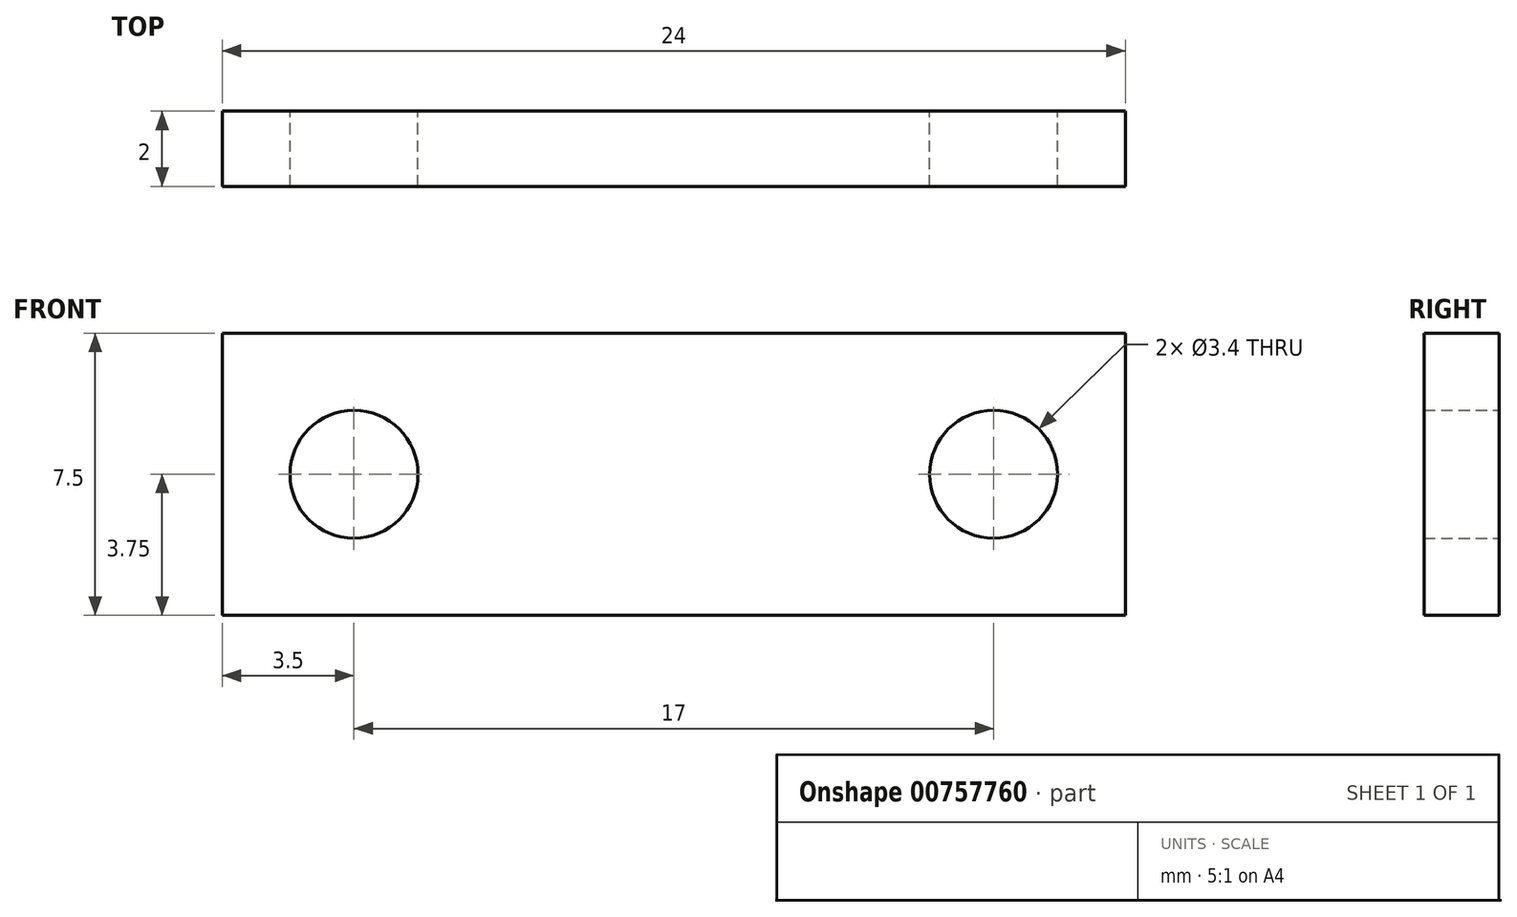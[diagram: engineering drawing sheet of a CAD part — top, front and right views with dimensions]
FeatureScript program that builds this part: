
annotation { "Feature Type Name" : "Feature", "Feature Type Description" : "" }
export const myFeature = defineFeature(function(context is Context, id is Id, definition is map)
    precondition{}
    {
        {
            var Q0;
            Q0=qCreatedBy(makeId("Front.planeOp"),FACE);
            var sketch = newSketch(context, id + "F0", { "sketchPlane" : qUnion([Q0])});
            skLineSegment(sketch, "E0.bottom", {"start": v(-12, 3.75) * mm, "end": v(12, 3.75) * mm});
            skLineSegment(sketch, "E0.top", {"start": v(-12, -3.75) * mm, "end": v(12, -3.75) * mm});
            skLineSegment(sketch, "E0.left", {"start": v(-12, 3.75) * mm, "end": v(-12, -3.75) * mm});
            skLineSegment(sketch, "E0.right", {"start": v(12, 3.75) * mm, "end": v(12, -3.75) * mm});
            skPoint(sketch, "E0.middle", {"position": v(0, 0) * mm});
            skPoint(sketch, "E1", {"position": v(-8.5, 0) * mm});
            skPoint(sketch, "E2", {"position": v(8.5, 0) * mm});
            skSolve(sketch);
        }
        {
            var Q0;
            Q0=makeQuery(id+"F0.imprint","IMPRINT",FACE,{"disambiguationData":[TD([[makeQuery(id+"F0.imprint","IMPRINT",EDGE,{"derivedFrom":sQuery(id+"F0.wireOp",EDGE,"E0.bottom")}),-1.0]])]});
            extrude(context, id + "F1", {"entities" : qUnion([Q0]), "depth" : 2 * mm, "offsetDistance" : 25 * mm});
        }
        {
            var Q0;
            Q0=sQuery(id+"F0.wireOp",VERTEX,"E1");
            var Q1;
            Q1=sQuery(id+"F0.wireOp",VERTEX,"E2");
            var Q2;
            Q2=makeQuery(id+"F1.opExtrude","SWEPT_BODY",BODY,{"disambiguationData":[OSD([sQuery(id+"F0.wireOp",EDGE,"E0.bottom"),sQuery(id+"F0.wireOp",EDGE,"E0.top"),sQuery(id+"F0.wireOp",EDGE,"E0.left"),sQuery(id+"F0.wireOp",EDGE,"E0.right")])]});
            hole(context, id + "F2", {"style" : HoleStyle.SIMPLE, "endStyle" : HoleEndStyle.THROUGH, "oppositeDirection" : true, "holeDiameter" : 3.4 * mm, "majorDiameter" : 5 * mm, "isTappedThrough" : true, "tappedDepth" : 12 * mm, "tapClearance" : 3, "startFromSketch" : true, "locations" : qUnion([Q0, Q1]), "scope" : qUnion([Q2])});
        }
    });
